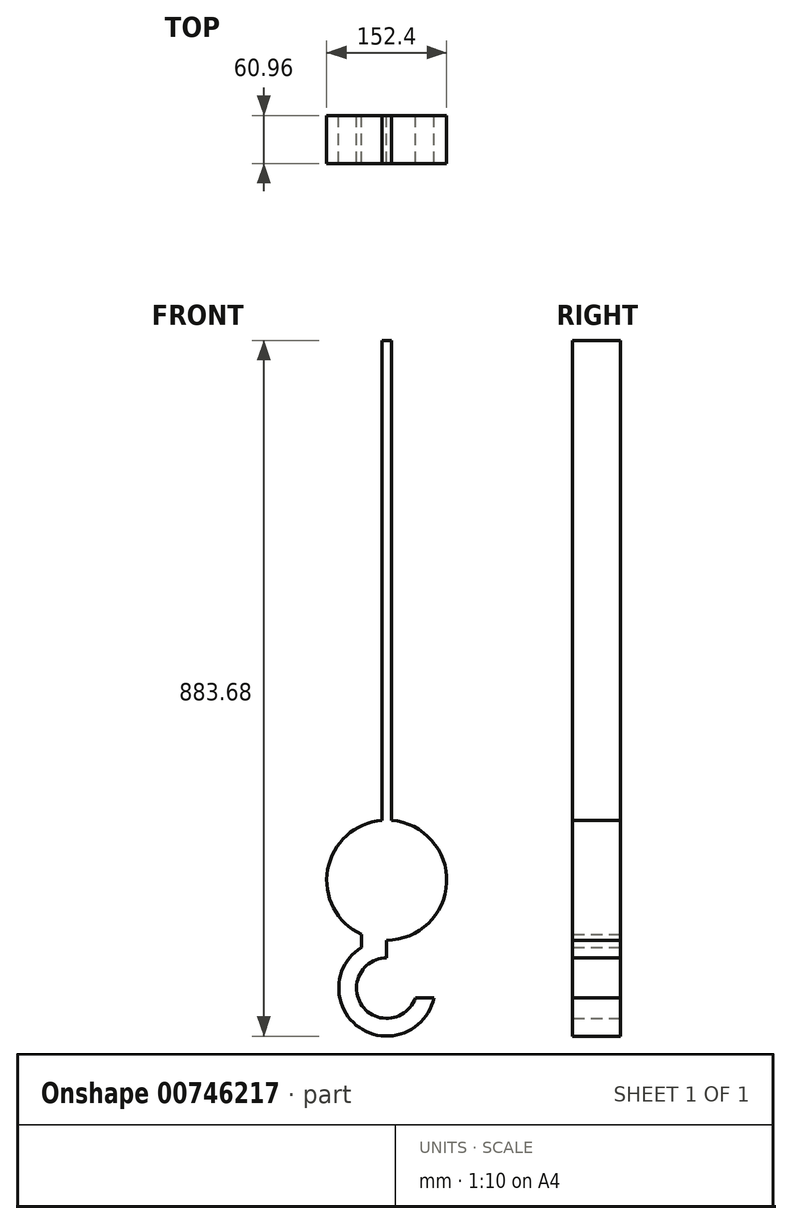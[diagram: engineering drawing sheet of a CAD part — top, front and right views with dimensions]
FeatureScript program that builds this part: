
annotation { "Feature Type Name" : "Feature", "Feature Type Description" : "" }
export const myFeature = defineFeature(function(context is Context, id is Id, definition is map)
    precondition{}
    {
        {
            var Q0;
            Q0=qCreatedBy(makeId("Front.planeOp"),FACE);
            var sketch = newSketch(context, id + "F0", { "sketchPlane" : qUnion([Q0])});
            skArc(sketch, "E0", {"start": v(-6.1, 75.96) * mm, "mid": v(-74.98, 13.56) * mm, "end": v(-32.32, -69) * mm});
            skArc(sketch, "E1", {"start": v(-32.32, -85.47) * mm, "mid": v(-34.83, -187.2) * mm, "end": v(59.7, -149.52) * mm});
            skArc(sketch, "E2.0", {"start": v(0, -98.76) * mm, "mid": v(-31.22, -159.52) * mm, "end": v(36.36, -149.52) * mm});
            skLineSegment(sketch, "E3", {"start": v(0, -76.2) * mm, "end": v(0, -98.76) * mm});
            skLineSegment(sketch, "E4", {"start": v(36.36, -149.52) * mm, "end": v(59.7, -149.52) * mm});
            skLineSegment(sketch, "E5.bottom", {"start": v(-6.1, 685.56) * mm, "end": v(6.1, 685.56) * mm});
            skLineSegment(sketch, "E5.left", {"start": v(-6.1, 685.56) * mm, "end": v(-6.1, 75.96) * mm});
            skLineSegment(sketch, "E5.right", {"start": v(6.1, 685.56) * mm, "end": v(6.1, 75.96) * mm});
            skLineSegment(sketch, "E6", {"start": v(-32.32, -69) * mm, "end": v(-32.32, -85.47) * mm});
            skLineSegment(sketch, "E7.trimOffspring", {"start": v(0, 75.96) * mm, "end": v(0, -420.12) * mm, "construction": true});
            skPoint(sketch, "E8.start.orphan", {"position": v(0, 329.47) * mm});
            skArc(sketch, "E9.trimOffspring", {"start": v(0, -76.2) * mm, "mid": v(76.14, -3.05) * mm, "end": v(6.1, 75.96) * mm});
            skSolve(sketch);
        }
        {
            var Q0;
            {var subQ2=sQuery(id+"F0.wireOp",EDGE,"E5.top");Q0=makeQuery(id+"F0.imprint","IMPRINT",FACE,{"disambiguationData":[TD([[makeQuery(id+"F0.imprint","IMPRINT",EDGE,{"derivedFrom":subQ2}),-1.0]])]});}
            var Q1;
            Q1=makeQuery(id+"F0.imprint","IMPRINT",FACE,{"disambiguationData":[TD([[makeQuery(id+"F0.imprint","IMPRINT",EDGE,{"derivedFrom":sQuery(id+"F0.wireOp",EDGE,"E5.bottom")}),-1.0]])]});
            var Q2;
            Q2=makeQuery(id+"F0.imprint","IMPRINT",FACE,{"disambiguationData":[TD([[makeQuery(id+"F0.imprint","IMPRINT",EDGE,{"derivedFrom":sQuery(id+"F0.wireOp",EDGE,"E1")}),1.0]])]});
            extrude(context, id + "F1", {"entities" : qUnion([Q0, Q1, Q2]), "depth" : 60.96 * mm, "offsetDistance" : 30.48 * mm});
        }
    });
